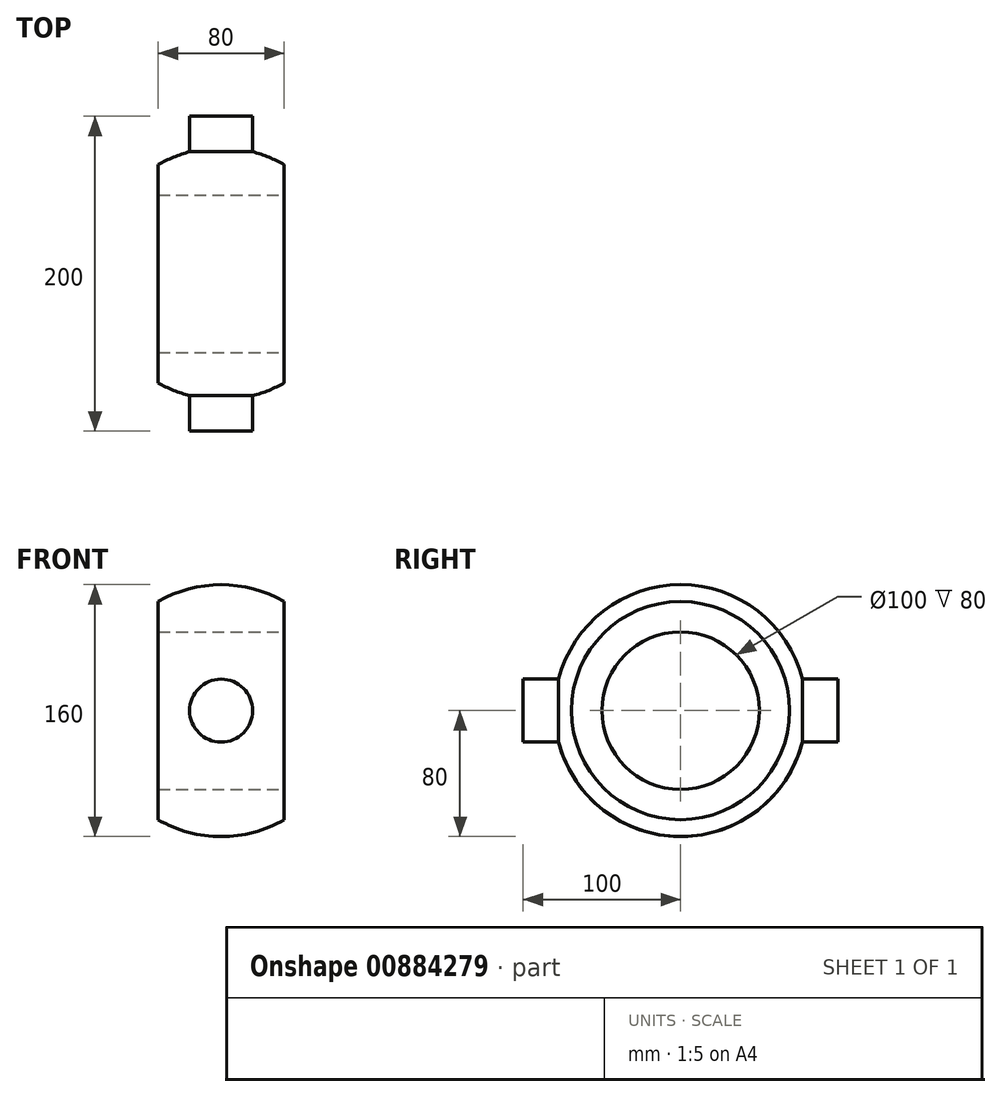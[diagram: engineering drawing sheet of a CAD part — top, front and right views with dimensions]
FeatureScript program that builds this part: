
annotation { "Feature Type Name" : "Feature", "Feature Type Description" : "" }
export const myFeature = defineFeature(function(context is Context, id is Id, definition is map)
    precondition{}
    {
        {
            var Q0;
            Q0=qCreatedBy(makeId("Front.planeOp"),FACE);
            var sketch = newSketch(context, id + "F0", { "sketchPlane" : qUnion([Q0])});
            skLineSegment(sketch, "E0", {"start": v(0, 0) * mm, "end": v(-380.18, 0) * mm, "construction": true});
            skLineSegment(sketch, "E1", {"start": v(-40, 80) * mm, "end": v(-40, 50) * mm});
            skLineSegment(sketch, "E2", {"start": v(-40, 50) * mm, "end": v(40, 50) * mm});
            skLineSegment(sketch, "E3", {"start": v(40, 50) * mm, "end": v(40, 80) * mm});
            skLineSegment(sketch, "E4", {"start": v(40, 80) * mm, "end": v(-40, 80) * mm});
            skLineSegment(sketch, "E5", {"start": v(0, 0) * mm, "end": v(0, 237.2) * mm, "construction": true});
            skSolve(sketch);
        }
        {
            var Q0;
            Q0 = qSketchRegion(id + "F0", true);
            var Q1;
            Q1=sQuery(id+"F0.wireOp",EDGE,"E0");
            revolve(context, id + "F1", {"surfaceOperationType" : NewSurfaceOperationType.NEW, "entities" : qUnion([Q0]), "axis" : qUnion([Q1]), "revolveType" : RevolveType.FULL});
        }
        {
            var Q0;
            Q0=qCreatedBy(makeId("Top.planeOp"),FACE);
            var sketch = newSketch(context, id + "F2", { "sketchPlane" : qUnion([Q0])});
            skLineSegment(sketch, "E6", {"start": v(0, 0) * mm, "end": v(0, 47.35) * mm, "construction": true});
            skArc(sketch, "E7", {"start": v(0, 80) * mm, "mid": v(-80, 0) * mm, "end": v(0, -80) * mm});
            skLineSegment(sketch, "E8", {"start": v(0, 80) * mm, "end": v(0, 110) * mm});
            skLineSegment(sketch, "E9", {"start": v(0, 110) * mm, "end": v(-110, 110) * mm});
            skLineSegment(sketch, "E10", {"start": v(-110, 110) * mm, "end": v(-110, -110) * mm});
            skLineSegment(sketch, "E11", {"start": v(-110, -110) * mm, "end": v(0, -110) * mm});
            skLineSegment(sketch, "E12", {"start": v(0, -110) * mm, "end": v(0, -80) * mm});
            skLineSegment(sketch, "E13", {"start": v(0, 0) * mm, "end": v(-174.57, 0) * mm, "construction": true});
            skSolve(sketch);
        }
        {
            var Q0;
            Q0 = qSketchRegion(id + "F2", true);
            var Q1;
            Q1=sQuery(id+"F2.wireOp",EDGE,"E6");
            revolve(context, id + "F3", {"operationType" : NewBodyOperationType.REMOVE, "surfaceOperationType" : NewSurfaceOperationType.NEW, "entities" : qUnion([Q0]), "axis" : qUnion([Q1]), "revolveType" : RevolveType.FULL, "oppositeDirection" : true});
        }
        {
            var Q0;
            Q0=qCreatedBy(makeId("Front.planeOp"),FACE);
            cPlane(context, id + "F4", {"entities" : qUnion([Q0]), "cplaneType" : CPlaneType.OFFSET, "offset" : 100 * mm, "width" : 150 * mm, "height" : 150 * mm});
        }
        {
            var Q0;
            Q0=qCreatedBy(id+"F4.planeOp",FACE);
            var sketch = newSketch(context, id + "F5", { "sketchPlane" : qUnion([Q0])});
            skCircle(sketch, "E14", {"center": v(0, 0) * mm, "radius": 20 * mm});
            skSolve(sketch);
        }
        {
            var Q0;
            Q0=makeQuery(id+"F5.imprint","IMPRINT",FACE,{"disambiguationData":[TD([[makeQuery(id+"F5.imprint","IMPRINT",EDGE,{"derivedFrom":sQuery(id+"F5.wireOp",EDGE,"E14")}),1.0]])]});
            extrude(context, id + "F6", {"entities" : qUnion([Q0]), "operationType" : NewBodyOperationType.ADD, "endBound" : BoundingType.UP_TO_NEXT, "oppositeDirection" : true, "depth" : 25 * mm, "offsetDistance" : 25 * mm});
        }
        {
            var Q0;
            Q0=makeQuery(id+"F1.opRevolve","SWEPT_BODY",BODY,{"disambiguationData":[OSD([sQuery(id+"F0.wireOp",EDGE,"E1"),sQuery(id+"F0.wireOp",EDGE,"E2"),sQuery(id+"F0.wireOp",EDGE,"E3"),sQuery(id+"F0.wireOp",EDGE,"E4")])]});
            var Q1;
            Q1=qCreatedBy(makeId("Front.planeOp"),FACE);
            mirror(context, id + "F7", {"operationType" : NewBodyOperationType.ADD, "entities" : qUnion([Q0]), "mirrorPlane" : qUnion([Q1])});
        }
    });
